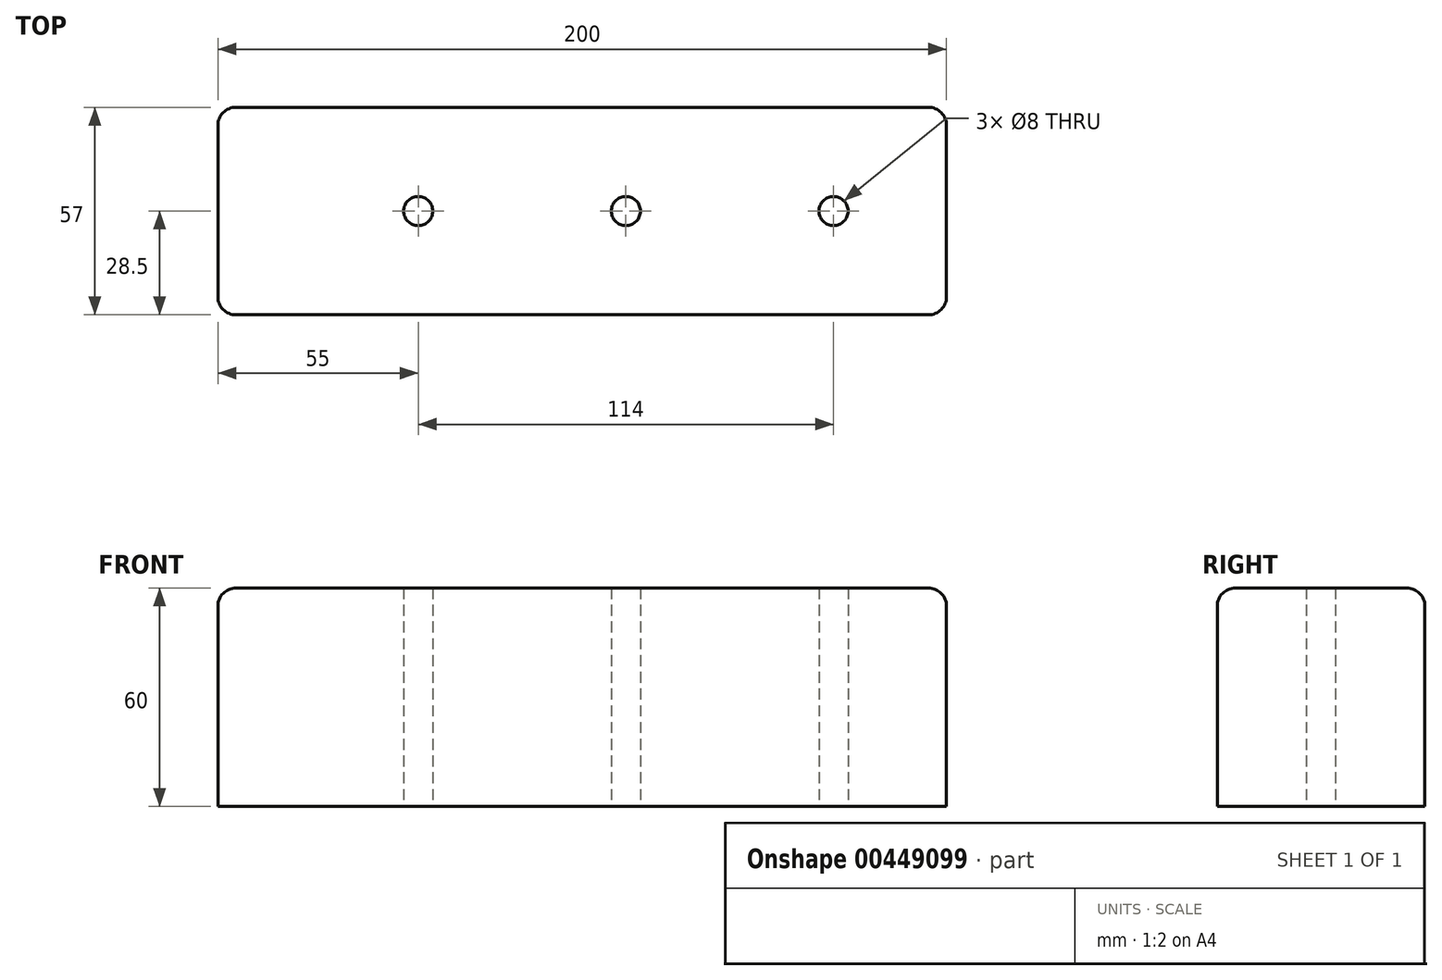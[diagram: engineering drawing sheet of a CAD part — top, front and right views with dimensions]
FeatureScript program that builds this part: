
annotation { "Feature Type Name" : "Feature", "Feature Type Description" : "" }
export const myFeature = defineFeature(function(context is Context, id is Id, definition is map)
    precondition{}
    {
        {
            var Q0;
            Q0=qCreatedBy(makeId("Top.planeOp"),FACE);
            var sketch = newSketch(context, id + "F0", { "sketchPlane" : qUnion([Q0])});
            skLineSegment(sketch, "E0.bottom", {"start": v(0, 0) * mm, "end": v(200, 0) * mm});
            skLineSegment(sketch, "E0.top", {"start": v(0, 57) * mm, "end": v(200, 57) * mm});
            skLineSegment(sketch, "E0.left", {"start": v(0, 0) * mm, "end": v(0, 57) * mm});
            skLineSegment(sketch, "E0.right", {"start": v(200, 0) * mm, "end": v(200, 57) * mm});
            skCircle(sketch, "E1", {"center": v(55, 28.5) * mm, "radius": 4 * mm});
            skCircle(sketch, "E2.1.0.0", {"center": v(112, 28.5) * mm, "radius": 4 * mm});
            skCircle(sketch, "E2.2.0.0", {"center": v(169, 28.5) * mm, "radius": 4 * mm});
            skLineSegment(sketch, "E2.direction1", {"start": v(55, 28.5) * mm, "end": v(112, 28.5) * mm, "construction": true});
            skSolve(sketch);
        }
        {
            var Q0;
            Q0=makeQuery(id+"F0.imprint","IMPRINT",FACE,{"disambiguationData":[TD([[makeQuery(id+"F0.imprint","IMPRINT",EDGE,{"derivedFrom":sQuery(id+"F0.wireOp",EDGE,"E0.bottom")}),1.0]])]});
            extrude(context, id + "F1", {"entities" : qUnion([Q0]), "depth" : 60 * mm});
        }
        {
            var Q0;
            Q0=makeQuery(id+"F1.opExtrude","SWEPT_EDGE",EDGE,{"disambiguationData":[OSD([sQuery(id+"F0.wireOp",EDGE,"E0.bottom"),sQuery(id+"F0.wireOp",EDGE,"E0.left")])]});
            var Q1;
            Q1=makeQuery(id+"F1.opExtrude","CAP_EDGE",EDGE,{"disambiguationData":[OSD([sQuery(id+"F0.wireOp",EDGE,"E0.bottom")])],"isStart":false});
            var Q2;
            Q2=makeQuery(id+"F1.opExtrude","CAP_EDGE",EDGE,{"disambiguationData":[OSD([sQuery(id+"F0.wireOp",EDGE,"E0.left")])],"isStart":false});
            var Q3;
            Q3=makeQuery(id+"F1.opExtrude","CAP_EDGE",EDGE,{"disambiguationData":[OSD([sQuery(id+"F0.wireOp",EDGE,"E0.top")])],"isStart":false});
            var Q4;
            Q4=makeQuery(id+"F1.opExtrude","CAP_EDGE",EDGE,{"disambiguationData":[OSD([sQuery(id+"F0.wireOp",EDGE,"E0.right")])],"isStart":false});
            var Q5;
            Q5=makeQuery(id+"F1.opExtrude","SWEPT_EDGE",EDGE,{"disambiguationData":[OSD([sQuery(id+"F0.wireOp",EDGE,"E0.bottom"),sQuery(id+"F0.wireOp",EDGE,"E0.right")])]});
            var Q6;
            Q6=makeQuery(id+"F1.opExtrude","SWEPT_EDGE",EDGE,{"disambiguationData":[OSD([sQuery(id+"F0.wireOp",EDGE,"E0.top"),sQuery(id+"F0.wireOp",EDGE,"E0.right")])]});
            var Q7;
            Q7=makeQuery(id+"F1.opExtrude","SWEPT_EDGE",EDGE,{"disambiguationData":[OSD([sQuery(id+"F0.wireOp",EDGE,"E0.top"),sQuery(id+"F0.wireOp",EDGE,"E0.left")])]});
            fillet(context, id + "F2", {"entities" : qUnion([Q0, Q1, Q2, Q3, Q4, Q5, Q6, Q7]), "radius" : 5 * mm, "tangentPropagation" : true, "allowEdgeOverflow" : false});
        }
    });
